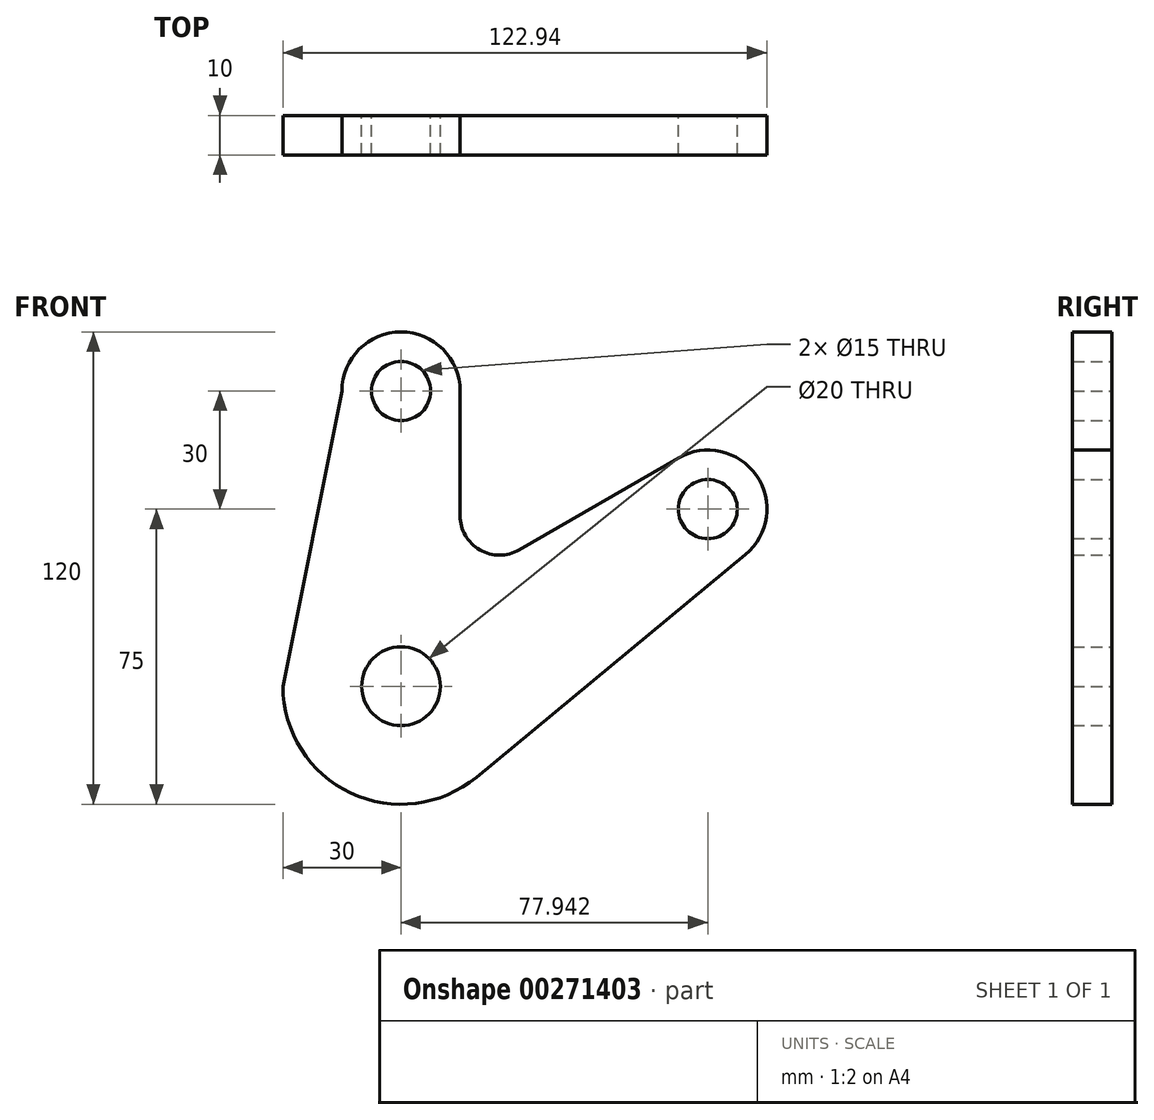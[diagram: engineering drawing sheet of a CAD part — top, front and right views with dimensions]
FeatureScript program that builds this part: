
annotation { "Feature Type Name" : "Feature", "Feature Type Description" : "" }
export const myFeature = defineFeature(function(context is Context, id is Id, definition is map)
    precondition{}
    {
        {
            var Q0;
            Q0=qCreatedBy(makeId("Front.planeOp"),FACE);
            var sketch = newSketch(context, id + "F0", { "sketchPlane" : qUnion([Q0])});
            skCircle(sketch, "E0", {"center": v(0, 0) * mm, "radius": 10 * mm});
            skArc(sketch, "E1", {"start": v(-30, 0) * mm, "mid": v(-12.77, -27.14) * mm, "end": v(19.12, -23.12) * mm});
            skCircle(sketch, "E2", {"center": v(0, 75) * mm, "radius": 7.5 * mm});
            skArc(sketch, "E3", {"start": v(15, 75) * mm, "mid": v(0, 90) * mm, "end": v(-15, 75) * mm});
            skLineSegment(sketch, "E4", {"start": v(-30, 0) * mm, "end": v(-15, 75) * mm});
            skLineSegment(sketch, "E5", {"start": v(15, 75) * mm, "end": v(15, 43.3) * mm});
            skArc(sketch, "E6", {"start": v(15, 43.3) * mm, "mid": v(20, 34.64) * mm, "end": v(30, 34.64) * mm});
            skLineSegment(sketch, "E7", {"start": v(0, 75) * mm, "end": v(0, 0) * mm, "construction": true});
            skLineSegment(sketch, "E8", {"start": v(0, 0) * mm, "end": v(77.94, 45) * mm, "construction": true});
            skCircle(sketch, "E9", {"center": v(77.94, 45) * mm, "radius": 7.5 * mm});
            skArc(sketch, "E10", {"start": v(70.44, 58) * mm, "mid": v(90.26, 53.56) * mm, "end": v(87.5, 33.44) * mm});
            skLineSegment(sketch, "E11", {"start": v(19.12, -23.12) * mm, "end": v(87.5, 33.44) * mm});
            skLineSegment(sketch, "E12", {"start": v(30, 34.64) * mm, "end": v(70.44, 58) * mm});
            skSolve(sketch);
        }
        {
            var Q0;
            Q0 = qSketchRegion(id + "F0", true);
            extrude(context, id + "F1", {"entities" : qUnion([Q0]), "depth" : 10 * mm});
        }
    });
